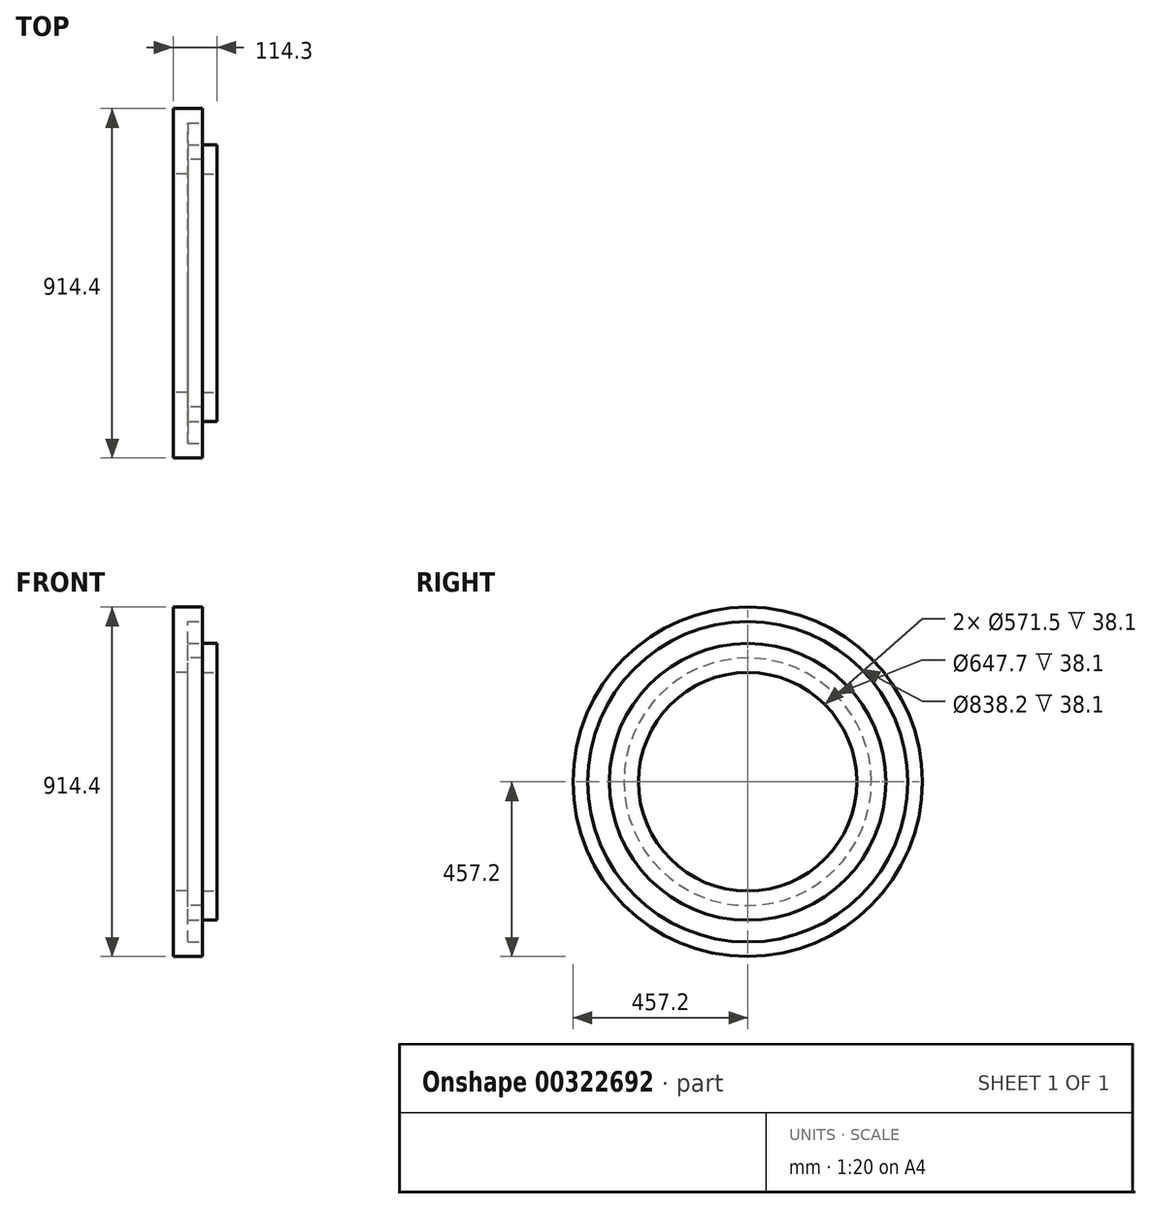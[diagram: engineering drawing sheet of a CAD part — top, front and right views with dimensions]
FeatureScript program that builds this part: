
annotation { "Feature Type Name" : "Feature", "Feature Type Description" : "" }
export const myFeature = defineFeature(function(context is Context, id is Id, definition is map)
    precondition{}
    {
        {
            var Q0;
            Q0=qCreatedBy(makeId("Right.planeOp"),FACE);
            var sketch = newSketch(context, id + "F0", { "sketchPlane" : qUnion([Q0])});
            skCircle(sketch, "E0", {"center": v(0, 0) * mm, "radius": 457.2 * mm});
            skCircle(sketch, "E1", {"center": v(0, 0) * mm, "radius": 419.1 * mm});
            skCircle(sketch, "E2", {"center": v(0, 0) * mm, "radius": 361.95 * mm});
            skCircle(sketch, "E3", {"center": v(0, 0) * mm, "radius": 323.85 * mm});
            skSolve(sketch);
        }
        {
            var Q0;
            Q0=makeQuery(id+"F0.imprint","IMPRINT",FACE,{"disambiguationData":[TD([[makeQuery(id+"F0.imprint","IMPRINT",EDGE,{"derivedFrom":sQuery(id+"F0.wireOp",EDGE,"E0")}),1.0]])]});
            var Q1;
            Q1=makeQuery(id+"F0.imprint","IMPRINT",FACE,{"disambiguationData":[TD([[makeQuery(id+"F0.imprint","IMPRINT",EDGE,{"derivedFrom":sQuery(id+"F0.wireOp",EDGE,"E1")}),1.0]])]});
            var Q2;
            Q2=makeQuery(id+"F0.imprint","IMPRINT",FACE,{"disambiguationData":[TD([[makeQuery(id+"F0.imprint","IMPRINT",EDGE,{"derivedFrom":sQuery(id+"F0.wireOp",EDGE,"E2")}),1.0]])]});
            extrude(context, id + "F1", {"entities" : qUnion([Q0, Q1, Q2]), "depth" : 76.2 * mm});
        }
        {
            var Q0;
            Q0=makeQuery(id+"F1.opExtrude","CAP_FACE",FACE,{"disambiguationData":[OSD([sQuery(id+"F0.wireOp",EDGE,"E0"),sQuery(id+"F0.wireOp",EDGE,"E3")])],"isStart":false});
            var sketch = newSketch(context, id + "F2", { "sketchPlane" : qUnion([Q0])});
            skCircle(sketch, "E4.0", {"center": v(0, 0) * mm, "radius": 361.95 * mm});
            skCircle(sketch, "E5.0", {"center": v(0, 0) * mm, "radius": 419.1 * mm});
            skSolve(sketch);
        }
        {
            var Q0;
            Q0=makeQuery(id+"F2.imprint","IMPRINT",FACE,{"disambiguationData":[TD([[makeQuery(id+"F2.imprint","IMPRINT",EDGE,{"derivedFrom":sQuery(id+"F2.wireOp",EDGE,"E4.0")}),-1.0]])]});
            extrude(context, id + "F3", {"entities" : qUnion([Q0]), "operationType" : NewBodyOperationType.REMOVE, "oppositeDirection" : true, "depth" : 38.1 * mm});
        }
        {
            var Q0;
            {var subQ0=sQuery(id+"F0.wireOp",EDGE,"E3");Q0=makeQuery(id+"F3.boolean.opBoolean","SPLIT",FACE,{"disambiguationData":[TD([makeQuery(id+"F1.opExtrude","SWEPT_FACE",FACE,{"disambiguationData":[OSD([subQ0])]})])],"derivedFrom":makeQuery(id+"F1.opExtrude","CAP_FACE",FACE,{"disambiguationData":[OSD([sQuery(id+"F0.wireOp",EDGE,"E0"),subQ0])],"isStart":false})});}
            extrude(context, id + "F4", {"entities" : qUnion([Q0]), "operationType" : NewBodyOperationType.ADD, "depth" : 38.1 * mm});
        }
        {
            var Q0;
            Q0=qCreatedBy(makeId("Right.planeOp"),FACE);
            var sketch = newSketch(context, id + "F5", { "sketchPlane" : qUnion([Q0])});
            skCircle(sketch, "E6", {"center": v(0, 0) * mm, "radius": 285.75 * mm});
            skCircle(sketch, "E7.0", {"center": v(0, 0) * mm, "radius": 323.85 * mm});
            skSolve(sketch);
        }
        {
            var Q0;
            Q0=makeQuery(id+"F5.imprint","IMPRINT",FACE,{"disambiguationData":[TD([[makeQuery(id+"F5.imprint","IMPRINT",EDGE,{"derivedFrom":sQuery(id+"F5.wireOp",EDGE,"E6")}),-1.0]])]});
            extrude(context, id + "F6", {"entities" : qUnion([Q0]), "operationType" : NewBodyOperationType.ADD, "depth" : 38.1 * mm});
        }
        {
            var Q0;
            Q0=makeQuery(id+"F4.opExtrude","CAP_FACE",FACE,{"disambiguationData":[OSD([sQuery(id+"F0.wireOp",EDGE,"E0"),sQuery(id+"F0.wireOp",EDGE,"E3")])],"isStart":false});
            var sketch = newSketch(context, id + "F7", { "sketchPlane" : qUnion([Q0])});
            skCircle(sketch, "E8.0", {"center": v(0, 0) * mm, "radius": 285.75 * mm});
            skCircle(sketch, "E9.0", {"center": v(0, 0) * mm, "radius": 323.85 * mm});
            skSolve(sketch);
        }
        {
            var Q0;
            Q0=makeQuery(id+"F7.imprint","IMPRINT",FACE,{"disambiguationData":[TD([[makeQuery(id+"F7.imprint","IMPRINT",EDGE,{"derivedFrom":sQuery(id+"F7.wireOp",EDGE,"E8.0")}),-1.0]])]});
            extrude(context, id + "F8", {"entities" : qUnion([Q0]), "operationType" : NewBodyOperationType.ADD, "oppositeDirection" : true, "depth" : 38.1 * mm});
        }
    });
